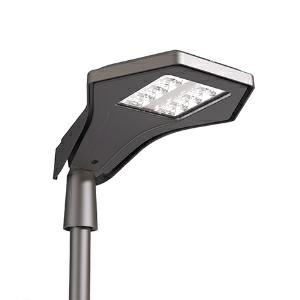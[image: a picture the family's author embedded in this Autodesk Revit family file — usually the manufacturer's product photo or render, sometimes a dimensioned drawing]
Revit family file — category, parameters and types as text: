
# Revit family: 3f_filippi_-_3f_manta_ampio_3f_filippi_-_7002_-_3f_manta_an_75-730_wide
name_source: partatom
category: Lighting Fixtures
units: mm (PartAtom-declared; Revit-internal decimal feet)

## family parameters
Cut with Voids When Loaded = No
Host = Face
Light Source = No
Part Type = Normal
Room Calculation Point = No
Round Connector Dimension = Use Diameter
Shared = No

## types (1)
- 3F Filippi - 3F Manta Ampio (1 x LED, 9717 lm, 78 W, 3000 K)
    Apparent Load = 78 VA
    Approval mark = CE
    CIE Flux Codes = 37 75 99 100 100
    Color Rendering = 70
    Color Temperature = 3000 K
    Control Gear = Electronic ballast
    Default Elevation = 1800 mm
    Description = ILLUMINOTECHNICAL
Luminous efficiency 100% (DLOR 100%, ULOR 0%).
Initial luminous flux of the luminaire 9717 lm.
Asymmetric distribution with wide bilateral.
BUG (Backlight, Uplight, Glare) IESNA TM-15: B2 U0 G2.
Luminous efficacy 125 lm/W.
Lifetime (L93/B10): 30000 h. (tq+25°C)
Lifetime (L90/B10): 50000 h. (tq+25°C)
Lifetime (L85/B10): 80000 h. (tq+25°C)
Lifetime (L80/B10): 100000 h. (tq+25°C)
Lifetime (L90/B20): 50000 h. (tq+45°C)
Sudden decreased luminous flux after 50000 hours: 0% (C0).
Photobiological safety in compliance with IEC/TR 62778: RG0 risk exempt, (IEC 62471).
In compliance with IEC/EN 62722-2-1 - IEC/EN 62717 standards.

SOURCE
Squared LED module 75W/730.
Source with special protection against aggressive chemically-volatile substances for standard LED technology.
Energy efficiency class (UE 2019/2020 - UE 2019/2015): D.
CIE 13.3 Colour rendering index: CRI >70 (R9 <50%).
IES TM-30 Fidelity Index: Rf = 72 Rg = 95.
CCT nominal colour temperature 3000 K.
Colour initial tolerance (MacAdam): SDCM 5.

MECHANICAL
Aerodynamically-shaped die-cast aluminium double-shell body for low wind resistance (frontal: 0.0446 m²; lateral: 0.0505 m²), equipped with fins to optimize the cooling of the internal components.
Shell closure using stainless steel screws on stainless steel bushings, with hinged opening for easy access to the wiring compartment, equipped with system against accidental closure.
Polyester powder coating with degreasing pre-treatment and phosphate layer deposit on the metal, UV stabilised, corrosion resistant, anthracite colour, salt spray resistance ISO 9227 >1000 h.
Parabolic cellular optics with total recovery, entirely made of semi-specular high reflection aluminium with titanium and magnesium surface treatment, to maintain optical performance over time.
Polyurethane foam seals, ecological, anti-aging, installed using a continuous automatic process with no joints.
VT extra transparent tempered glass diffuser, 4 mm thick, non-combustible, with Heat Soak Test (HST) thermal treatment, which drastically reduces the risk of spontaneous breakage.
Stainless steel internal and external screws.
Luminaire with limited surface temperature. - D - (EN 60598-2-24)
Dimensions: 660x440 mm, height 166 mm. Weight 10.89 kg.
IP66 protection degree.
Mechanical strength to impacts IK08 (5 joule).
Glow-wire test resistance 960°C.

ELECTRICAL
Halogen Free electronic wiring 230V-50/60Hz, power factor 0.97, THD <25%, constant output current, class I, 1 driver.
Power of the luminaire 78 W.
ENEC - CE.
SAFE FLICKER: PstLM=<1 and SVM=<0.4 (IEC TR 61547-1 and IEC TR 63158), to ensure a more comfortable and safe light.
Ambient temperature from -20°C to +45°C.
Temperature class T6 max 85°C.
Safety break switch to shut off the power supply when opening the device.
Insulation voltage 6kV via Sourge Protector.
SPD type 2+3 (combined) device to protect against voltage surges up to 10 kV in common and differential mode.
Thermal protection of the LED module via NTC sensor (Negative Temperature Coefficient).
M20x1.5 IP68 nylon cable gland for feeding input (cables with an min-max diameter 6-13mm).
Pressure compensating valve with anti-condensation effect.
Relative humidity UR: <85%.

INSTALLATION
Post-top / arm / wall.
Installation with always necessary "Pole fixing" accessory (see accessories).
All accessories dedicated to this product are available on the Catalog and on our website www.3F-Filippi.com.

ACCESSORIES
Pole mount in die-cast aluminium with the same paint treatment as the body (for Ø 60 mm and Ø 76 mm poles) equipped with special teeth for adjusting the inclination on the head of the device by ± 20° with an adjustment pitch of 5°.
Possibility of installing on vertical pole (pole head) and horizontal pole (arm).
Mounting on the device using the supplied stainless steel screws on self-locking stainless steel nuts.
A0439 - Pole mounting diameter 60 mm.
A0440 - Pole mounting diameter 76 mm.

APPLICATIONS
Outdoor environments, general lighting, work and roadway lighting, transit areas and building perimeters, parking lots, trade fairs.
Control of light pollution, in accordance with the legislative requirements in force.

LIGHT MANAGEMENT
Upon request, the appliance can be supplied with "Virtual Midnight" programming.

WARNING
Luminaire designed for disposal/recycling at end-of-life.
Replaceable (LED only) light source by a professional. Replaceable control gear by a professional.
    Height = 166 mm
    Lamp = 1 x LED
    Lamp Light Flux = 9717 lm
    Lamp Power = 78 W
    Lamp count = 1
    Length = 660 mm
    Lifetime = 50000 h
    Luminous efficacy = 125 lm/W
    Manufacturer = 3F Filippi
    ModVariant = No
    Model = 3F Filippi - 7002 - 3F Manta AN 75-730 WIDE
    Mounting Place = Pole
    Mounting Type = Pole top
    Number of Poles = 1
    OnlyDefault = Yes
    Power Factor = 1
    Product Name = 3F Filippi - 3F Manta Ampio
    Product group = street luminaire
    ProductGroupID = 15
    Protection Class = Protection class I
    Protection Degree = IP 66
    RLX_Detail_Level = 1
    RLX_Emergency_Light_Flux = 0 lm
    RLX_Emergency_Type = 0
    RLX_Emergency_Type_DB = No
    RlxData = <blob elided: 225405 chars, md5=5642debf>
    Socket = socket
    Standby Power = 0 W
    System Light Flux = 9717 lm
    System Power = 78 W
    Type Comments = Product without accessories
    Type Image = 3ffilippi_3f_manta_wide.jpg
    URL = http://relux.com
    VarID = ---
    Voltage = 0 V
    Weight = 0.00 kg
    Width = 440 mm

## geometry (parser evidence)
native form markers: Blend x4, Sweep x15
no freeform markers — native parametric forms only
